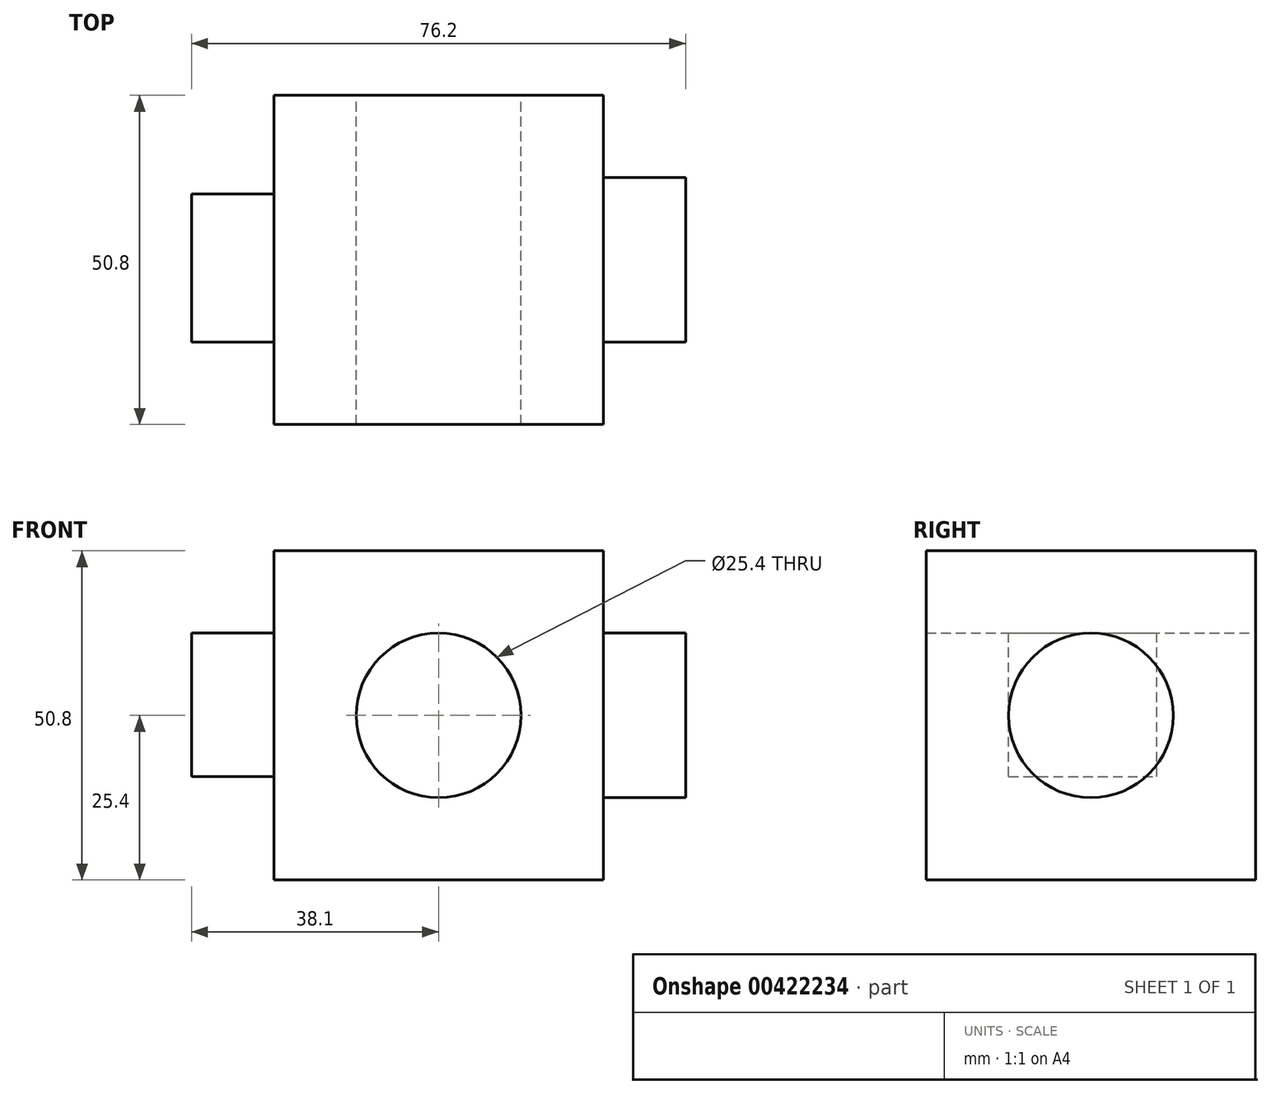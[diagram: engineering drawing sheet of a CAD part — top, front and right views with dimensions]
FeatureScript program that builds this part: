
annotation { "Feature Type Name" : "Feature", "Feature Type Description" : "" }
export const myFeature = defineFeature(function(context is Context, id is Id, definition is map)
    precondition{}
    {
        {
            var Q0;
            Q0=qCreatedBy(makeId("Front.planeOp"),FACE);
            var sketch = newSketch(context, id + "F0", { "sketchPlane" : qUnion([Q0])});
            skLineSegment(sketch, "E0.bottom", {"start": v(0, 0) * mm, "end": v(50.8, 0) * mm});
            skLineSegment(sketch, "E0.top", {"start": v(0, -50.8) * mm, "end": v(50.8, -50.8) * mm});
            skLineSegment(sketch, "E0.left", {"start": v(0, 0) * mm, "end": v(0, -50.8) * mm});
            skLineSegment(sketch, "E0.right", {"start": v(50.8, 0) * mm, "end": v(50.8, -50.8) * mm});
            skSolve(sketch);
        }
        {
            var Q0;
            Q0 = qSketchRegion(id + "F0", true);
            extrude(context, id + "F1", {"entities" : qUnion([Q0]), "depth" : 50.8 * mm});
        }
        {
            var Q0;
            Q0=makeQuery(id+"F1.opExtrude","CAP_FACE",FACE,{"disambiguationData":[OSD([sQuery(id+"F0.wireOp",EDGE,"E0.bottom"),sQuery(id+"F0.wireOp",EDGE,"E0.top"),sQuery(id+"F0.wireOp",EDGE,"E0.left"),sQuery(id+"F0.wireOp",EDGE,"E0.right")])],"isStart":true});
            var sketch = newSketch(context, id + "F2", { "sketchPlane" : qUnion([Q0])});
            skCircle(sketch, "E1", {"center": v(-25.4, -25.4) * mm, "radius": 12.7 * mm});
            skSolve(sketch);
        }
        {
            var Q0;
            Q0 = qSketchRegion(id + "F2", true);
            extrude(context, id + "F3", {"entities" : qUnion([Q0]), "operationType" : NewBodyOperationType.REMOVE, "oppositeDirection" : true, "depth" : 50.8 * mm});
        }
        {
            var Q0;
            Q0=makeQuery(id+"F1.opExtrude","SWEPT_FACE",FACE,{"disambiguationData":[OSD([sQuery(id+"F0.wireOp",EDGE,"E0.left")])]});
            var sketch = newSketch(context, id + "F4", { "sketchPlane" : qUnion([Q0])});
            skLineSegment(sketch, "E2.bottom", {"start": v(38.1, -34.83) * mm, "end": v(15.21, -34.83) * mm});
            skLineSegment(sketch, "E2.top", {"start": v(38.1, -12.7) * mm, "end": v(15.21, -12.7) * mm});
            skLineSegment(sketch, "E2.left", {"start": v(38.1, -34.83) * mm, "end": v(38.1, -12.7) * mm});
            skLineSegment(sketch, "E2.right", {"start": v(15.21, -34.83) * mm, "end": v(15.21, -12.7) * mm});
            skSolve(sketch);
        }
        {
            var Q0;
            Q0 = qSketchRegion(id + "F4", true);
            extrude(context, id + "F5", {"entities" : qUnion([Q0]), "operationType" : NewBodyOperationType.ADD, "depth" : 12.7 * mm});
        }
        {
            var Q0;
            Q0=makeQuery(id+"F1.opExtrude","SWEPT_FACE",FACE,{"disambiguationData":[OSD([sQuery(id+"F0.wireOp",EDGE,"E0.right")])]});
            var sketch = newSketch(context, id + "F6", { "sketchPlane" : qUnion([Q0])});
            skCircle(sketch, "E3", {"center": v(-25.4, -25.4) * mm, "radius": 12.7 * mm});
            skSolve(sketch);
        }
        {
            var Q0;
            Q0 = qSketchRegion(id + "F6", true);
            extrude(context, id + "F7", {"entities" : qUnion([Q0]), "operationType" : NewBodyOperationType.ADD, "depth" : 12.7 * mm});
        }
    });
